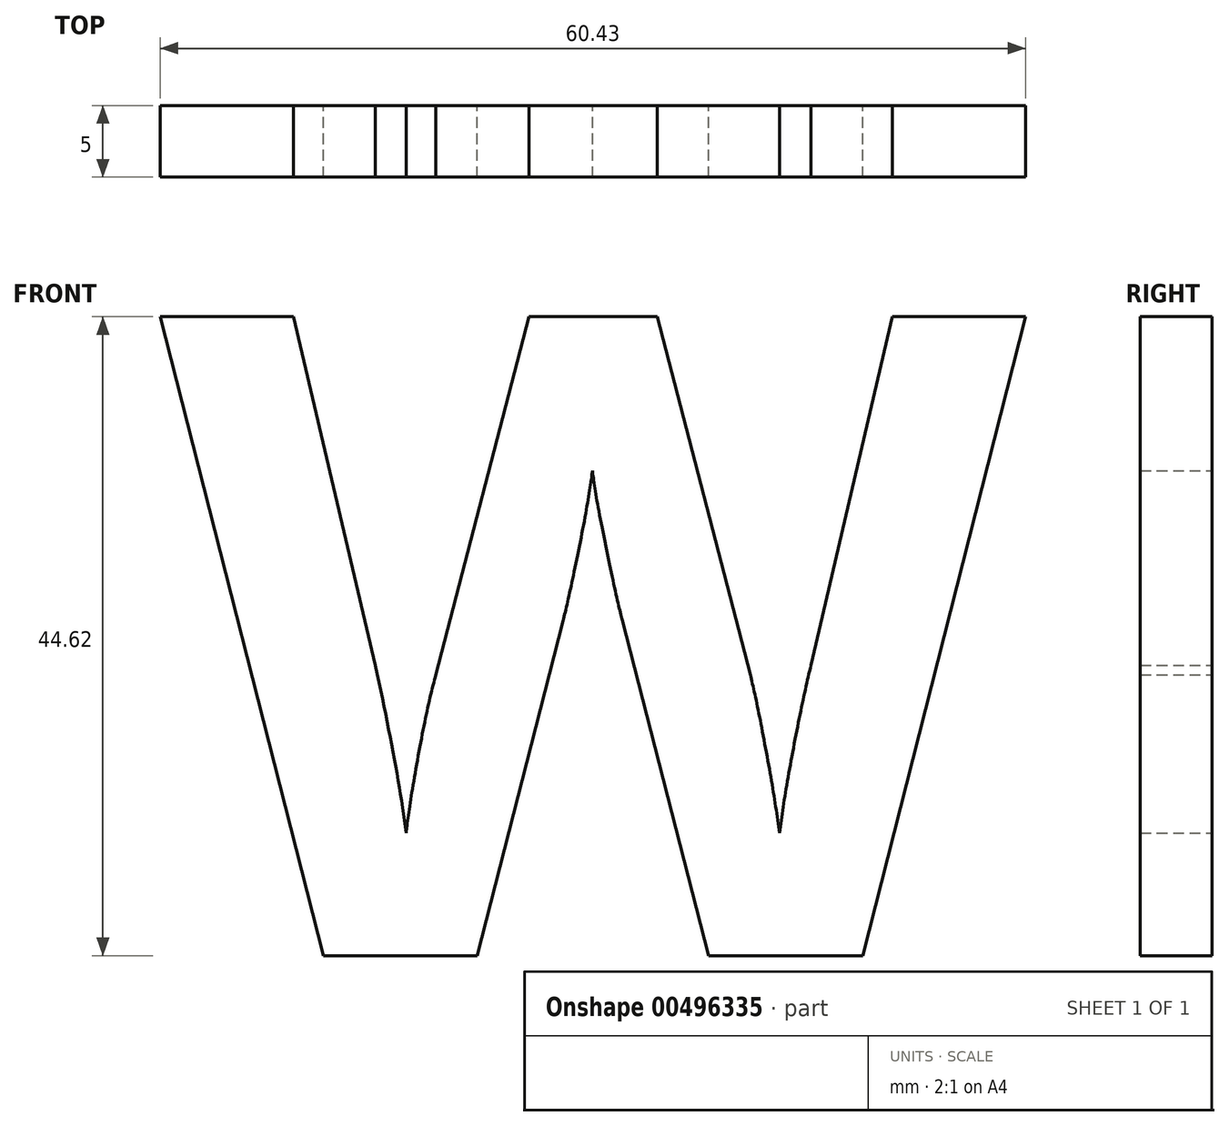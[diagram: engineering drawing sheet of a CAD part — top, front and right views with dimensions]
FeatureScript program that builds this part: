
annotation { "Feature Type Name" : "Feature", "Feature Type Description" : "" }
export const myFeature = defineFeature(function(context is Context, id is Id, definition is map)
    precondition{}
    {
        {
            var Q0;
            Q0=qCreatedBy(makeId("Front.planeOp"),FACE);
            var sketch = newSketch(context, id + "F0", { "sketchPlane" : qUnion([Q0])});
            skText(sketch, "E0", { "text": "W", "fontName": "OpenSans-Bold.ttf"});
            const initialGuessF0  = {"E0": [-0.0539, 0.0112, 1, 0, 0.045]};
            skSetInitialGuess(sketch, initialGuessF0);
            skSolve(sketch);
        }
        {
            var Q0;
            Q0=makeQuery(id+"F0.imprint","IMPRINT",FACE,{"disambiguationData":[TD([[makeQuery(id+"F0.imprint","IMPRINT",EDGE,{"derivedFrom":sQuery(id+"F0.wireOp",EDGE,"E0.sketch_text.stroke-0")}),-1.0]])]});
            extrude(context, id + "F1", {"entities" : qUnion([Q0]), "depth" : 5 * mm});
        }
    });
